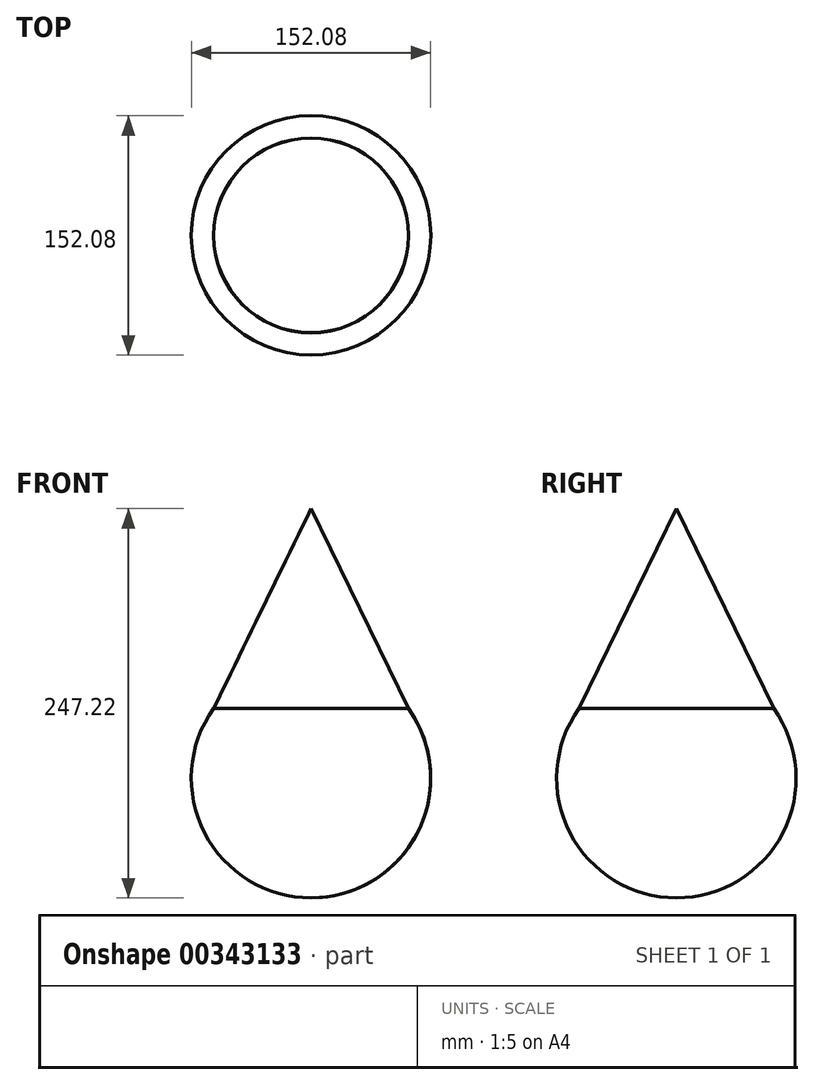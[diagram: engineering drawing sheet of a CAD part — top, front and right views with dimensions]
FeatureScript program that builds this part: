
annotation { "Feature Type Name" : "Feature", "Feature Type Description" : "" }
export const myFeature = defineFeature(function(context is Context, id is Id, definition is map)
    precondition{}
    {
        {
            var Q0;
            Q0=qCreatedBy(makeId("Front.planeOp"),FACE);
            var sketch = newSketch(context, id + "F0", { "sketchPlane" : qUnion([Q0])});
            skArc(sketch, "E0", {"start": v(0, -76.04) * mm, "mid": v(76.04, 0) * mm, "end": v(0, 76.04) * mm});
            skLineSegment(sketch, "E1", {"start": v(0, 76.04) * mm, "end": v(0, -76.04) * mm});
            skSolve(sketch);
        }
        {
            var Q0;
            Q0=makeQuery(id+"F0.imprint","IMPRINT",FACE,{"disambiguationData":[TD([[makeQuery(id+"F0.imprint","IMPRINT",EDGE,{"derivedFrom":sQuery(id+"F0.wireOp",EDGE,"E0")}),1.0]])]});
            var Q1;
            Q1=sQuery(id+"F0.wireOp",EDGE,"E1");
            revolve(context, id + "F1", {"entities" : qUnion([Q0]), "axis" : qUnion([Q1]), "revolveType" : RevolveType.FULL});
        }
        {
            var Q0;
            Q0=qCreatedBy(makeId("Front.planeOp"),FACE);
            var sketch = newSketch(context, id + "F2", { "sketchPlane" : qUnion([Q0])});
            skLineSegment(sketch, "E2.bottom", {"start": v(-76.79, 44.18) * mm, "end": v(75.27, 44.18) * mm});
            skLineSegment(sketch, "E2.top", {"start": v(-76.79, 76.79) * mm, "end": v(75.27, 76.79) * mm});
            skLineSegment(sketch, "E2.left", {"start": v(-76.79, 44.18) * mm, "end": v(-76.79, 76.79) * mm});
            skLineSegment(sketch, "E2.right", {"start": v(75.27, 44.18) * mm, "end": v(75.27, 76.79) * mm});
            skSolve(sketch);
        }
        {
            var Q0;
            Q0=makeQuery(id+"F2.imprint","IMPRINT",FACE,{"disambiguationData":[TD([[makeQuery(id+"F2.imprint","IMPRINT",EDGE,{"derivedFrom":sQuery(id+"F2.wireOp",EDGE,"E2.bottom")}),1.0]])]});
            extrude(context, id + "F3", {"entities" : qUnion([Q0]), "operationType" : NewBodyOperationType.REMOVE, "endBound" : BoundingType.SYMMETRIC, "oppositeDirection" : true, "depth" : 127 * mm});
        }
        {
            var Q0;
            Q0=makeQuery(id+"F3.boolean.opBoolean","COPY",FACE,{"derivedFrom":makeQuery(id+"F3.opExtrude","SWEPT_FACE",FACE,{"disambiguationData":[OSD([sQuery(id+"F2.wireOp",EDGE,"E2.bottom")])]})});
            var sketch = newSketch(context, id + "F4", { "sketchPlane" : qUnion([Q0])});
            skCircle(sketch, "E3", {"center": v(0, 0) * mm, "radius": 61.82 * mm});
            skSolve(sketch);
        }
        {
            var Q0;
            Q0=makeQuery(id+"F4.imprint","IMPRINT",FACE,{"disambiguationData":[TD([[makeQuery(id+"F4.imprint","IMPRINT",EDGE,{"derivedFrom":sQuery(id+"F4.wireOp",EDGE,"E3")}),1.0]])]});
            var sketch = newSketch(context, id + "F5", { "sketchPlane" : qUnion([Q0])});
            skCircle(sketch, "E4", {"center": v(0, 0) * mm, "radius": 61.73 * mm});
            skSolve(sketch);
        }
        {
            var Q0;
            Q0=makeQuery(id+"F5.imprint","IMPRINT",FACE,{"disambiguationData":[TD([[makeQuery(id+"F5.imprint","IMPRINT",EDGE,{"derivedFrom":sQuery(id+"F5.wireOp",EDGE,"E4")}),1.0]])]});
            cPlane(context, id + "F6", {"entities" : qUnion([Q0]), "cplaneType" : CPlaneType.OFFSET, "offset" : 127 * mm, "width" : 152.4 * mm, "height" : 152.4 * mm});
        }
        {
            var Q0;
            Q0=qCreatedBy(id+"F6.planeOp",FACE);
            var sketch = newSketch(context, id + "F7", { "sketchPlane" : qUnion([Q0])});
            skPoint(sketch, "E5", {"position": v(0, 0) * mm});
            skSolve(sketch);
        }
        {
            var Q0;
            Q0=makeQuery(id+"F4.imprint","IMPRINT",FACE,{"disambiguationData":[TD([[makeQuery(id+"F4.imprint","IMPRINT",EDGE,{"derivedFrom":sQuery(id+"F4.wireOp",EDGE,"E3")}),1.0]])]});
            var Q1;
            Q1=sQuery(id+"F7.wireOp",VERTEX,"E5");
            loft(context, id + "F8", {"sheetProfilesArray" : [{ "sheetProfileEntities" : qUnion([Q0]) }, { "sheetProfileEntities" : qUnion([Q1]) }]});
        }
    });
